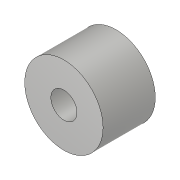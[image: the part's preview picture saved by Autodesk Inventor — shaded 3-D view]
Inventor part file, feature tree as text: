
AUTODESK INVENTOR PART (.ipt)
format: ipt  version: 2018.3 (Build 223284000, 284)  size: 83,968 bytes
history: native  units: in
note: dims shown in document units (in); Inventor stores cm internally (conversion verified against a paired STEP export)
features: extrude x1, sketch x1
ambient origin geometry x8: Origin, YZ Plane, XZ Plane, XY Plane, X Axis, Y Axis, Z Axis, Center Point
bodies: Solid1 (feature_tree)
feature tree (2):
  extrude  "Extrusion1"  Depth=0.25in
  sketch  "Sketch1"  dims[d0=0.125in d1=0.375in d2=0.25in d3=0.0in]
